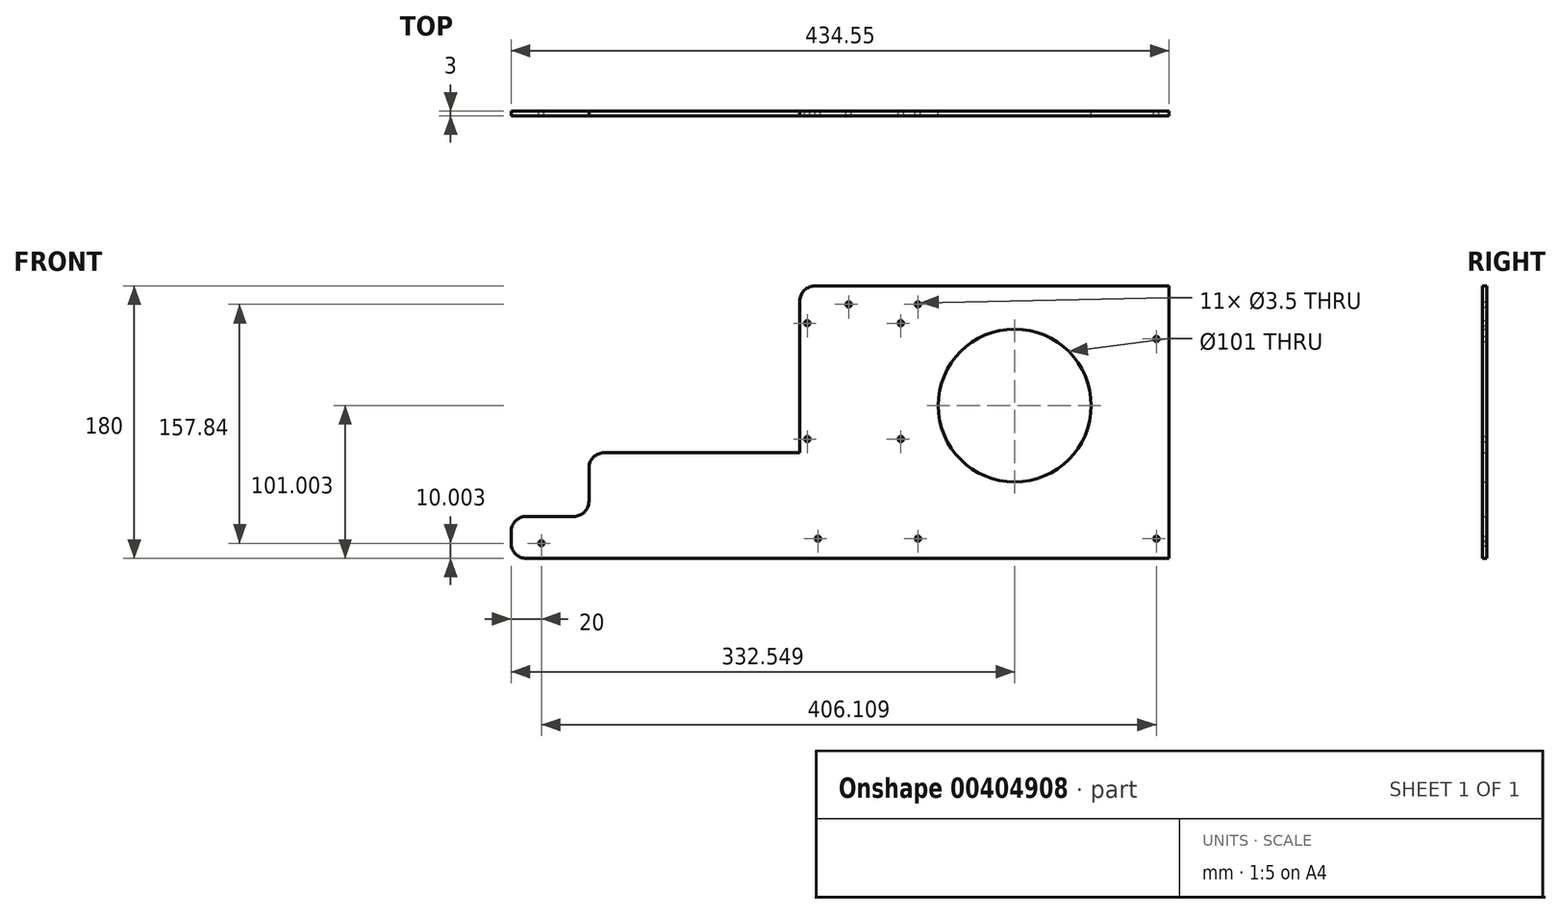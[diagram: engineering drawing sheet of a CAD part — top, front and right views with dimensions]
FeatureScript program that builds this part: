
annotation { "Feature Type Name" : "Feature", "Feature Type Description" : "" }
export const myFeature = defineFeature(function(context is Context, id is Id, definition is map)
    precondition{}
    {
        {
            var Q0;
            Q0=qCreatedBy(makeId("Front.planeOp"),FACE);
            var sketch = newSketch(context, id + "F0", { "sketchPlane" : qUnion([Q0])});
            skLineSegment(sketch, "E0.top", {"start": v(-163.49, -78.87) * mm, "end": v(271.06, -78.87) * mm});
            skLineSegment(sketch, "E0.right", {"start": v(271.06, 101.13) * mm, "end": v(271.06, -78.87) * mm});
            skLineSegment(sketch, "E1.bottom", {"start": v(25.22, 99.13) * mm, "end": v(269.06, 99.13) * mm});
            skLineSegment(sketch, "E1.top", {"start": v(25.22, -73.87) * mm, "end": v(269.06, -73.87) * mm});
            skLineSegment(sketch, "E1.left", {"start": v(25.22, 99.13) * mm, "end": v(25.22, -73.87) * mm});
            skLineSegment(sketch, "E1.right", {"start": v(269.06, 99.13) * mm, "end": v(269.06, -73.87) * mm});
            skLineSegment(sketch, "E2", {"start": v(262.62, 99.13) * mm, "end": v(262.62, -73.87) * mm, "construction": true});
            skLineSegment(sketch, "E3", {"start": v(25.22, 88.97) * mm, "end": v(269.06, 88.97) * mm, "construction": true});
            skLineSegment(sketch, "E4", {"start": v(25.22, -65.87) * mm, "end": v(269.06, -65.87) * mm, "construction": true});
            skLineSegment(sketch, "E5", {"start": v(59.42, 99.13) * mm, "end": v(59.42, -73.87) * mm, "construction": true});
            skCircle(sketch, "E6", {"center": v(59.42, 88.97) * mm, "radius": 1.75 * mm});
            skCircle(sketch, "E7", {"center": v(105.14, 88.97) * mm, "radius": 1.75 * mm});
            skCircle(sketch, "E8", {"center": v(262.62, 66.12) * mm, "radius": 1.75 * mm});
            skCircle(sketch, "E9", {"center": v(262.62, -65.87) * mm, "radius": 1.75 * mm});
            skCircle(sketch, "E10", {"center": v(39.1, -65.87) * mm, "radius": 1.75 * mm});
            skCircle(sketch, "E11", {"center": v(105.14, -65.87) * mm, "radius": 1.75 * mm});
            skLineSegment(sketch, "E12.top", {"start": v(-157.49, -51.17) * mm, "end": v(-127.49, -51.17) * mm});
            skCircle(sketch, "E13", {"center": v(-143.49, -68.87) * mm, "radius": 1.75 * mm});
            skLineSegment(sketch, "E14", {"start": v(-163.49, -51.17) * mm, "end": v(-112.11, -51.17) * mm});
            skLineSegment(sketch, "E15", {"start": v(-112.11, -51.17) * mm, "end": v(-112.11, -9.07) * mm});
            skLineSegment(sketch, "E16", {"start": v(-112.11, -9.07) * mm, "end": v(27.12, -9.07) * mm});
            skLineSegment(sketch, "E17", {"start": v(27.12, -9.07) * mm, "end": v(27.12, 101.13) * mm});
            skLineSegment(sketch, "E18", {"start": v(-163.49, -78.87) * mm, "end": v(-163.49, -51.17) * mm});
            skLineSegment(sketch, "E19", {"start": v(27.12, 101.13) * mm, "end": v(271.06, 101.13) * mm});
            skCircle(sketch, "E20", {"center": v(169.06, 22.13) * mm, "radius": 50.5 * mm});
            skLineSegment(sketch, "E21.bottom", {"start": v(32.12, 76.56) * mm, "end": v(93.84, 76.56) * mm});
            skLineSegment(sketch, "E21.top", {"start": v(32.12, -0.04) * mm, "end": v(93.84, -0.04) * mm});
            skLineSegment(sketch, "E21.left", {"start": v(32.12, 76.56) * mm, "end": v(32.12, -0.04) * mm});
            skLineSegment(sketch, "E21.right", {"start": v(93.84, 76.56) * mm, "end": v(93.84, -0.04) * mm});
            skCircle(sketch, "E22", {"center": v(93.84, 76.56) * mm, "radius": 1.75 * mm});
            skCircle(sketch, "E23", {"center": v(93.84, -0.04) * mm, "radius": 1.75 * mm});
            skCircle(sketch, "E24", {"center": v(32.12, -0.04) * mm, "radius": 1.75 * mm});
            skCircle(sketch, "E25", {"center": v(32.12, 76.56) * mm, "radius": 1.75 * mm});
            skSolve(sketch);
        }
        {
            var Q0;
            Q0=makeQuery(id+"F0.imprint","IMPRINT",FACE,{"disambiguationData":[TD([[makeQuery(id+"F0.imprint","IMPRINT",EDGE,{"derivedFrom":sQuery(id+"F0.wireOp",EDGE,"E0.top")}),1.0]])]});
            var Q1;
            {var subQ14=sQuery(id+"F0.wireOp",EDGE,"E1.top");Q1=makeQuery(id+"F0.imprint","IMPRINT",FACE,{"disambiguationData":[TD([[makeQuery(id+"F0.imprint","IMPRINT",EDGE,{"derivedFrom":subQ14}),1.0]])]});}
            var Q2;
            {var subQ5=sQuery(id+"F0.wireOp",EDGE,"E25");var subQ13=sQuery(id+"F0.wireOp",EDGE,"E21.bottom");var subQ14=makeQuery(id+"F0.imprint","INTERSECT",VERTEX,{"derivedFrom":[subQ13,subQ5]});Q2=makeQuery(id+"F0.imprint","IMPRINT",FACE,{"disambiguationData":[TD([[makeQuery(id+"F0.imprint","IMPRINT",EDGE,{"disambiguationData":[TD([[subQ14,-1.0]])],"derivedFrom":subQ13}),-1.0]])]});}
            extrude(context, id + "F1", {"entities" : qUnion([Q0, Q1, Q2]), "depth" : 3 * mm});
        }
        {
            var Q0;
            Q0=makeQuery(id+"F1.opExtrude","SWEPT_EDGE",EDGE,{"disambiguationData":[OSD([sQuery(id+"F0.wireOp",EDGE,"E14"),sQuery(id+"F0.wireOp",EDGE,"E18")])]});
            var Q1;
            Q1=makeQuery(id+"F1.opExtrude","SWEPT_EDGE",EDGE,{"disambiguationData":[OSD([sQuery(id+"F0.wireOp",EDGE,"E15"),sQuery(id+"F0.wireOp",EDGE,"E16")])]});
            var Q2;
            Q2=makeQuery(id+"F1.opExtrude","SWEPT_EDGE",EDGE,{"disambiguationData":[OSD([sQuery(id+"F0.wireOp",EDGE,"E14"),sQuery(id+"F0.wireOp",EDGE,"E15")])]});
            var Q3;
            Q3=makeQuery(id+"F1.opExtrude","SWEPT_EDGE",EDGE,{"disambiguationData":[OSD([sQuery(id+"F0.wireOp",EDGE,"E0.top"),sQuery(id+"F0.wireOp",EDGE,"E18")])]});
            var Q4;
            Q4=makeQuery(id+"F1.opExtrude","SWEPT_EDGE",EDGE,{"disambiguationData":[OSD([sQuery(id+"F0.wireOp",EDGE,"E17"),sQuery(id+"F0.wireOp",EDGE,"E19")])]});
            fillet(context, id + "F2", {"entities" : qUnion([Q0, Q1, Q2, Q3, Q4]), "radius" : 10 * mm, "tangentPropagation" : true, "allowEdgeOverflow" : false});
        }
    });
